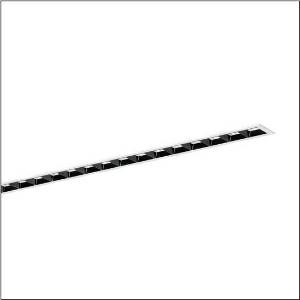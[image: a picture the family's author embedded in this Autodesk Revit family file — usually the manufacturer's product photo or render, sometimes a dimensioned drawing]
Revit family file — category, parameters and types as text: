
# Revit family: silica_r__21_51mx14dj43wb_69e6
name_source: partatom
category: Lighting Fixtures
units: mm (PartAtom-declared; Revit-internal decimal feet)

## family parameters
Cut with Voids When Loaded = No
Host = Face
Light Source = No
Part Type = Normal
Room Calculation Point = No
Round Connector Dimension = Use Diameter
Shared = No

## types (1)
- --- (1 x LED, 3240 lm, 22.8 W, 4000K)
    Apparent Load = 23 VA
    CIE Flux Codes = 74 94 99 100 100
    Color Rendering = 80
    Color Temperature = 4000K
    Default Elevation = 1800 mm
    Description = Silica® 21, office luminaire, primary light control with darklight reflector, of PMMA, black, light emission: direct distribution, primary light characteristic: asymmetric, installation type: recessed, LED, rated luminous flux: 3.240lm, luminous efficacy: 142lm/W, light colour: 840, colour temperature: 4000K, control gear: DALI 2, with terminal, 3+2-pole, max. 2.5mm², mains connection: 220..240V, AC, 50/60Hz, rated input power: 22.8W, luminaire housing, of aluminium, traffic white (RAL 9016), length: 900mm, width: 79mm, height: 53mm, protection rating (complete): IP20, insulation class (complete): insulation class I (protective earthing), certification: CE, permissible operating ambient temperature: 0..+35°C, standard: EN 50419, packaging unit: 1 piece
    Height = 0 mm  [stored 0 ft]
    Lamp = 1 x LED
    Lamp Light Flux = 3240 lm
    Lamp Power = 22.8 W
    Lamp count = 1
    Length = 927 mm
    Luminous efficacy = 142 lm/W
    Manufacturer = Siteco
    ModVariant = No
    Model = 51MX14DJ43WB
    Mounting Place = Ceiling
    Mounting Type = Recessed
    Number of Poles = 1
    OnlyDefault = Yes
    Power Factor = 1
    Product Name = Silica® 21
    Product group = office luminaire | ceiling recessed
    ProductGroupID = 400
    Protection Class = Protection class I
    Protection Degree = IP 20
    RLX_Detail_Level = 1
    RLX_Emergency_Light_Flux = 0 lm
    RLX_Emergency_Type = 0
    RLX_Emergency_Type_DB = No
    RlxData = <blob elided: 17945 chars, md5=6c8551b4>
    Socket = socket
    Standby Power = 0 W
    System Light Flux = 3240 lm
    System Power = 23 W
    Type Comments = factory setting: luminous flux: 100 % | dim-lin: 254 | 207 mA
    Type Image = l_1335880.jpg
    URL = http://relux.com
    VarID = @adj_032855
    Voltage = 0 V
    Weight = 0.00 kg
    Width = 79 mm

note: [stored X ft] marks values corroborated as IEEE doubles in the binary element streams (Revit-internal decimal feet)

## geometry (parser evidence)
native form markers: Blend x4, Sweep x13
no freeform markers — native parametric forms only
